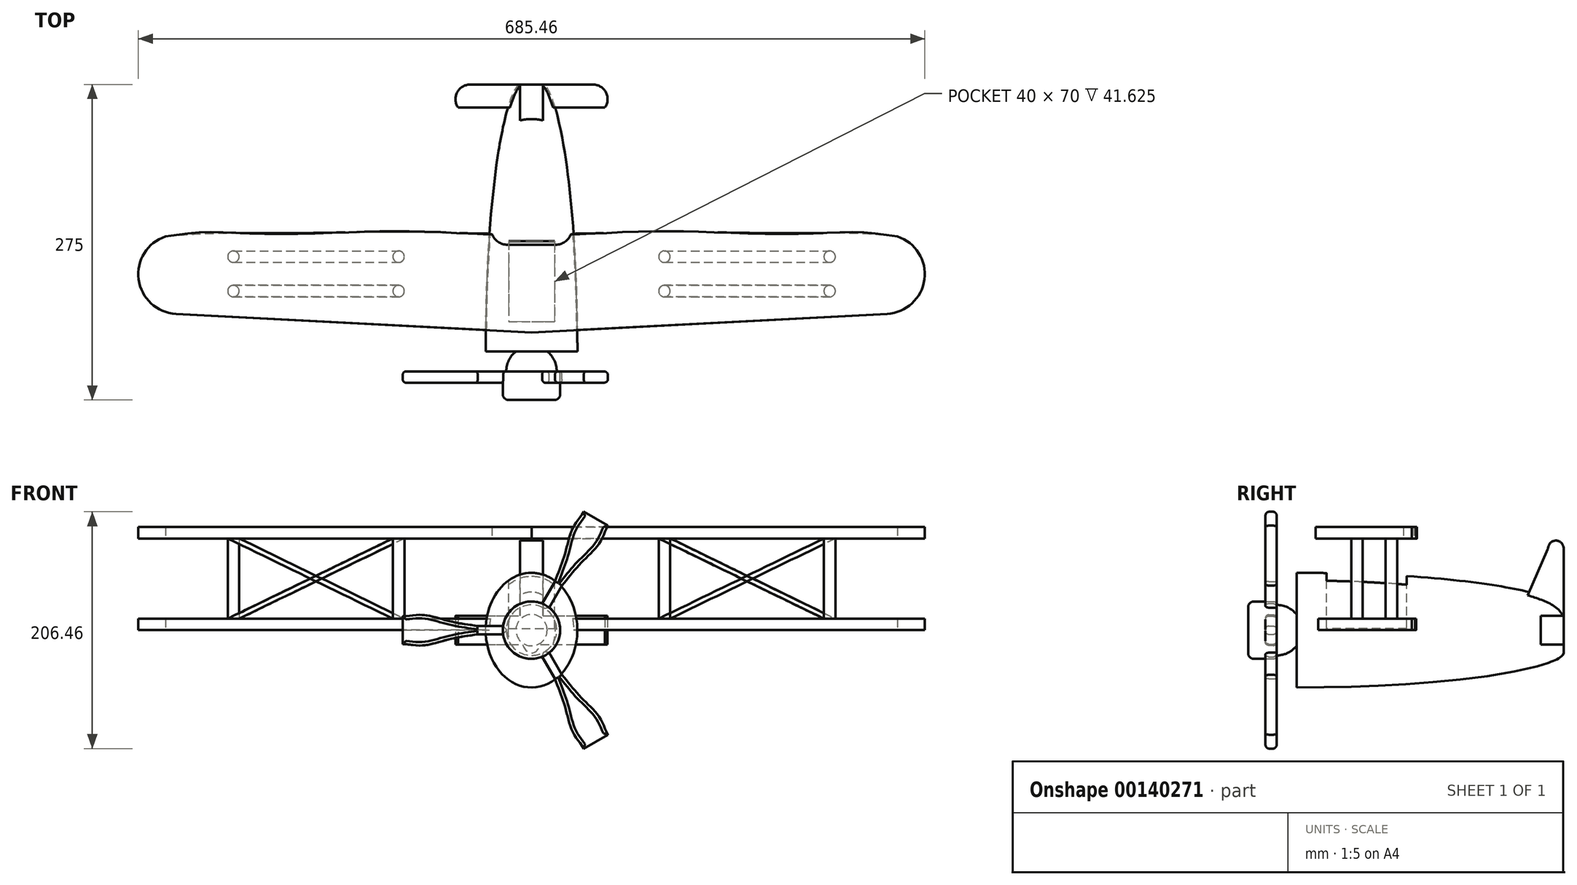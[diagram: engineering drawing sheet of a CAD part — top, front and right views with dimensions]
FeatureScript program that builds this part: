
annotation { "Feature Type Name" : "Feature", "Feature Type Description" : "" }
export const myFeature = defineFeature(function(context is Context, id is Id, definition is map)
    precondition{}
    {
        {
            var Q0;
            Q0=qCreatedBy(makeId("Front.planeOp"),FACE);
            var sketch = newSketch(context, id + "F0", { "sketchPlane" : qUnion([Q0])});
            skCircle(sketch, "E0", {"center": v(0, 0) * mm, "radius": 25 * mm});
            skSolve(sketch);
        }
        {
            var Q0;
            Q0=makeQuery(id+"F0.imprint","IMPRINT",FACE,{"disambiguationData":[TD([[makeQuery(id+"F0.imprint","IMPRINT",EDGE,{"derivedFrom":sQuery(id+"F0.wireOp",EDGE,"E0")}),1.0]])]});
            extrude(context, id + "F1", {"entities" : qUnion([Q0]), "depth" : 25 * mm});
        }
        {
            var Q0;
            Q0=makeQuery(id+"F1.opExtrude","CAP_EDGE",EDGE,{"disambiguationData":[OSD([sQuery(id+"F0.wireOp",EDGE,"E0")])],"isStart":false});
            fillet(context, id + "F2", {"entities" : qUnion([Q0]), "radius" : 5 * mm, "tangentPropagation" : true, "allowEdgeOverflow" : false});
        }
        {
            var Q0;
            Q0=qCreatedBy(makeId("Front.planeOp"),FACE);
            var sketch = newSketch(context, id + "F3", { "sketchPlane" : qUnion([Q0])});
            skArc(sketch, "E1.0", {"start": v(-24.75, 3.55) * mm, "mid": v(-25, 0) * mm, "end": v(-24.75, -3.55) * mm});
            skLineSegment(sketch, "E2", {"start": v(-124.47, 0) * mm, "end": v(45.62, 0) * mm, "construction": true});
            skLineSegment(sketch, "E3", {"start": v(-112.22, 0) * mm, "end": v(-112.22, 12.1) * mm});
            skLineSegment(sketch, "E4", {"start": v(-24.75, 3.55) * mm, "end": v(-47, 3.55) * mm});
            skFitSpline(sketch, "E5", {"points": [v(-47, 3.55) * mm, v(-69.47, 7.36) * mm, v(-95.13, 13.3) * mm, v(-112.22, 12.1) * mm], "startDerivative": vector(-60.76, 10.94) * mm, "endDerivative": vector(-54.66, -0.71) * mm});
            skLineSegment(sketch, "E6.MirrorCS", {"start": v(-112.22, 0) * mm, "end": v(-112.22, -12.1) * mm});
            skLineSegment(sketch, "E7.MirrorCS", {"start": v(-24.75, -3.55) * mm, "end": v(-47, -3.55) * mm});
            skFitSpline(sketch, "E8.MirrorCS", {"points": [v(-47, -3.55) * mm, v(-69.47, -7.36) * mm, v(-95.13, -13.3) * mm, v(-112.22, -12.1) * mm], "startDerivative": vector(-60.76, -10.94) * mm, "endDerivative": vector(-54.66, 0.71) * mm});
            skSolve(sketch);
        }
        {
            var Q0;
            Q0=makeQuery(id+"F3.imprint","IMPRINT",FACE,{"disambiguationData":[TD([[makeQuery(id+"F3.imprint","IMPRINT",EDGE,{"derivedFrom":sQuery(id+"F3.wireOp",EDGE,"E1.0")}),-1.0]])]});
            extrude(context, id + "F4", {"entities" : qUnion([Q0]), "operationType" : NewBodyOperationType.ADD, "depth" : 10 * mm});
        }
        {
            var Q0;
            Q0=makeQuery(id+"F4.opExtrude","CAP_EDGE",EDGE,{"disambiguationData":[OSD([sQuery(id+"F3.wireOp",EDGE,"E5")])],"isStart":false});
            var Q1;
            Q1=makeQuery(id+"F4.opExtrude","CAP_EDGE",EDGE,{"disambiguationData":[OSD([sQuery(id+"F3.wireOp",EDGE,"E4")])],"isStart":false});
            var Q2;
            Q2=makeQuery(id+"F4.opExtrude","CAP_EDGE",EDGE,{"disambiguationData":[OSD([sQuery(id+"F3.wireOp",EDGE,"E8.MirrorCS")])],"isStart":false});
            var Q3;
            Q3=makeQuery(id+"F4.opExtrude","CAP_EDGE",EDGE,{"disambiguationData":[OSD([sQuery(id+"F3.wireOp",EDGE,"E7.MirrorCS")])],"isStart":false});
            var Q4;
            Q4=makeQuery(id+"F4.opExtrude","CAP_EDGE",EDGE,{"disambiguationData":[OSD([sQuery(id+"F3.wireOp",EDGE,"E3"),sQuery(id+"F3.wireOp",EDGE,"E6.MirrorCS")])],"isStart":false});
            fillet(context, id + "F5", {"entities" : qUnion([Q0, Q1, Q2, Q3, Q4]), "radius" : 3 * mm, "tangentPropagation" : true, "allowEdgeOverflow" : false});
        }
        {
            var Q0;
            Q0=makeQuery(id+"F4.boolean.opBoolean","MERGE",FACE,{"derivedFrom":[makeQuery(id+"F1.opExtrude","CAP_FACE",FACE,{"disambiguationData":[OSD([sQuery(id+"F0.wireOp",EDGE,"E0")])],"isStart":true}),makeQuery(id+"F4.opExtrude","CAP_FACE",FACE,{"disambiguationData":[OSD([sQuery(id+"F3.wireOp",EDGE,"E1.0"),sQuery(id+"F3.wireOp",EDGE,"E3"),sQuery(id+"F3.wireOp",EDGE,"E4"),sQuery(id+"F3.wireOp",EDGE,"E5"),sQuery(id+"F3.wireOp",EDGE,"E6.MirrorCS"),sQuery(id+"F3.wireOp",EDGE,"E7.MirrorCS"),sQuery(id+"F3.wireOp",EDGE,"E8.MirrorCS")])],"isStart":true})]});
            fillet(context, id + "F6", {"entities" : qUnion([Q0]), "radius" : 3 * mm, "tangentPropagation" : true, "allowEdgeOverflow" : false});
        }
        {
            var Q0;
            Q0=qCreatedBy(makeId("Top.planeOp"),FACE);
            var sketch = newSketch(context, id + "F7", { "sketchPlane" : qUnion([Q0])});
            skLineSegment(sketch, "E9", {"start": v(0, -64.65) * mm, "end": v(0, 40.57) * mm});
            skSolve(sketch);
        }
        {
            var Q0;
            Q0=makeQuery(id+"F1.opExtrude","SWEPT_BODY",BODY,{"disambiguationData":[OSD([sQuery(id+"F0.wireOp",EDGE,"E0")])]});
            var Q1;
            Q1=sQuery(id+"F7.wireOp",EDGE,"E9");
            circularPattern(context, id + "F8", {"entities" : qUnion([Q0]), "axis" : qUnion([Q1]), "angle" : 360 * degree, "instanceCount" : 3, "equalSpace" : true});
        }
        {
            var Q0;
            Q0=qCreatedBy(makeId("Right.planeOp"),FACE);
            var sketch = newSketch(context, id + "F9", { "sketchPlane" : qUnion([Q0])});
            skLineSegment(sketch, "E10", {"start": v(0, 0) * mm, "end": v(17.25, 0) * mm});
            skLineSegment(sketch, "E11", {"start": v(0, -22) * mm, "end": v(0, 22) * mm, "construction": true});
            skArc(sketch, "E12", {"start": v(0, -22) * mm, "mid": v(9.58, -19.8) * mm, "end": v(17.25, -13.65) * mm});
            skLineSegment(sketch, "E13", {"start": v(17.25, 0) * mm, "end": v(17.25, -13.65) * mm});
            skLineSegment(sketch, "E14", {"start": v(0, 0) * mm, "end": v(0, -22) * mm});
            skSolve(sketch);
        }
        {
            var Q0;
            Q0=makeQuery(id+"F9.imprint","IMPRINT",FACE,{"disambiguationData":[TD([[makeQuery(id+"F9.imprint","IMPRINT",EDGE,{"derivedFrom":sQuery(id+"F9.wireOp",EDGE,"E10")}),-1.0]])]});
            var Q1;
            Q1=sQuery(id+"F9.wireOp",EDGE,"E10");
            revolve(context, id + "F10", {"operationType" : NewBodyOperationType.ADD, "entities" : qUnion([Q0]), "axis" : qUnion([Q1]), "revolveType" : RevolveType.FULL});
        }
        {
            var Q0;
            Q0=makeQuery(id+"F10.opRevolve","SWEPT_FACE",FACE,{"disambiguationData":[OSD([sQuery(id+"F9.wireOp",EDGE,"E13")])]});
            var sketch = newSketch(context, id + "F11", { "sketchPlane" : qUnion([Q0])});
            skEllipse(sketch, "E15", {"center": v(0, 0) * mm, "majorRadius": 50 * mm, "minorRadius": 40 * mm, "majorAxis": v(0, 1)});
            skSolve(sketch);
        }
        {
            var Q0;
            Q0=qCreatedBy(makeId("Front.planeOp"),FACE);
            cPlane(context, id + "F12", {"entities" : qUnion([Q0]), "cplaneType" : CPlaneType.OFFSET, "offset" : 250 * mm, "oppositeDirection" : true, "width" : 150 * mm, "height" : 150 * mm});
        }
        {
            var Q0;
            Q0=qCreatedBy(id+"F12.planeOp",FACE);
            var sketch = newSketch(context, id + "F13", { "sketchPlane" : qUnion([Q0])});
            skEllipse(sketch, "E16", {"center": v(0, 0) * mm, "majorRadius": 20 * mm, "minorRadius": 10 * mm, "majorAxis": v(0, 1)});
            skSolve(sketch);
        }
        {
            var Q1;
            Q1 = qSketchRegion(id + "F11", true);
            var Q2;
            Q2 = qSketchRegion(id + "F13", true);
            loft(context, id + "F14", {"operationType" : NewBodyOperationType.ADD, "startCondition" : LoftEndDerivativeType.NORMAL_TO_PROFILE, "startMagnitude" : 2, "endCondition" : LoftEndDerivativeType.TANGENT_TO_PROFILE, "endMagnitude" : 1, "sheetProfilesArray" : [{ "sheetProfileEntities" : qUnion([Q1]) }, { "sheetProfileEntities" : qUnion([Q2]) }]});
        }
        {
            var Q0;
            Q0=qCreatedBy(makeId("Top.planeOp"),FACE);
            var sketch = newSketch(context, id + "F15", { "sketchPlane" : qUnion([Q0])});
            skFitSpline(sketch, "E17.0", {"points": [v(-10, 250) * mm, v(-3.33, 250) * mm, v(3.33, 250) * mm, v(10, 250) * mm], "construction": true});
            skLineSegment(sketch, "E18", {"start": v(0, 273.6) * mm, "end": v(0, 147.57) * mm, "construction": true});
            skLineSegment(sketch, "E19", {"start": v(0, 250) * mm, "end": v(-53.66, 250) * mm});
            skLineSegment(sketch, "E20", {"start": v(-63.9, 229.96) * mm, "end": v(0, 229.96) * mm});
            skArc(sketch, "E21", {"start": v(-53.66, 250) * mm, "mid": v(-64.91, 243.11) * mm, "end": v(-63.9, 229.96) * mm});
            skFitSpline(sketch, "E22.MirrorCS", {"points": [v(10, 250) * mm, v(3.33, 250) * mm, v(-3.33, 250) * mm, v(-10, 250) * mm], "construction": true});
            skArc(sketch, "E23.MirrorCS", {"start": v(53.66, 250) * mm, "mid": v(64.91, 243.11) * mm, "end": v(63.9, 229.96) * mm});
            skLineSegment(sketch, "E24.MirrorCS", {"start": v(0, 250) * mm, "end": v(53.66, 250) * mm});
            skLineSegment(sketch, "E25.MirrorCS", {"start": v(63.9, 229.96) * mm, "end": v(0, 229.96) * mm});
            skSolve(sketch);
        }
        {
            var Q0;
            Q0=makeQuery(id+"F15.imprint","IMPRINT",FACE,{"disambiguationData":[TD([[makeQuery(id+"F15.imprint","IMPRINT",EDGE,{"derivedFrom":sQuery(id+"F15.wireOp",EDGE,"E19")}),1.0]])]});
            extrude(context, id + "F16", {"entities" : qUnion([Q0]), "operationType" : NewBodyOperationType.ADD, "endBound" : BoundingType.SYMMETRIC, "depth" : 25 * mm});
        }
        {
            var Q0;
            Q0=qCreatedBy(makeId("Right.planeOp"),FACE);
            var sketch = newSketch(context, id + "F17", { "sketchPlane" : qUnion([Q0])});
            skFitSpline(sketch, "E26.0", {"points": [v(250, 12.5) * mm, v(250, 15) * mm, v(250, 17.5) * mm, v(250, 20) * mm], "construction": true});
            skFitSpline(sketch, "E27.0", {"points": [v(250, -12.5) * mm, v(250, -15) * mm, v(250, -17.5) * mm, v(250, -20) * mm], "construction": true});
            skLineSegment(sketch, "E28.0", {"start": v(250, 12.5) * mm, "end": v(250, -12.5) * mm, "construction": true});
            skLineSegment(sketch, "E29", {"start": v(250, 12.5) * mm, "end": v(250, 71.39) * mm});
            skPoint(sketch, "E29.endSnap0", {"position": v(250, 0) * mm});
            skArc(sketch, "E30", {"start": v(250, 71.39) * mm, "mid": v(243.6, 78.12) * mm, "end": v(236.55, 72.06) * mm});
            skLineSegment(sketch, "E31", {"start": v(236.16, 70.57) * mm, "end": v(215.93, 23.8) * mm});
            skLineSegment(sketch, "E32", {"start": v(250, 12.5) * mm, "end": v(209.86, 12.5) * mm});
            skLineSegment(sketch, "E33", {"start": v(215.74, 23.4) * mm, "end": v(209.86, 12.5) * mm});
            skPoint(sketch, "E34.visualSharp", {"position": v(236.51, 71.39) * mm});
            skArc(sketch, "E34.filletArc", {"start": v(236.16, 70.57) * mm, "mid": v(236.41, 71.3) * mm, "end": v(236.55, 72.06) * mm});
            skPoint(sketch, "E35.visualSharp", {"position": v(215.85, 23.6) * mm});
            skArc(sketch, "E35.filletArc", {"start": v(215.74, 23.4) * mm, "mid": v(215.84, 23.6) * mm, "end": v(215.93, 23.8) * mm});
            skSolve(sketch);
        }
        {
            var Q0;
            Q0=makeQuery(id+"F17.imprint","IMPRINT",FACE,{"disambiguationData":[TD([[makeQuery(id+"F17.imprint","IMPRINT",EDGE,{"derivedFrom":sQuery(id+"F17.wireOp",EDGE,"E29")}),1.0]])]});
            extrude(context, id + "F18", {"entities" : qUnion([Q0]), "operationType" : NewBodyOperationType.ADD, "endBound" : BoundingType.SYMMETRIC, "depth" : 20 * mm});
        }
        {
            var Q0;
            Q0=qCreatedBy(makeId("Top.planeOp"),FACE);
            cPlane(context, id + "F19", {"entities" : qUnion([Q0]), "cplaneType" : CPlaneType.OFFSET, "offset" : 70 * mm, "width" : 150 * mm, "height" : 150 * mm});
        }
        {
            var Q0;
            Q0=qCreatedBy(id+"F19.planeOp",FACE);
            var sketch = newSketch(context, id + "F20", { "sketchPlane" : qUnion([Q0])});
            skLineSegment(sketch, "E36.bottom", {"start": v(-20, 113.36) * mm, "end": v(20, 113.36) * mm});
            skLineSegment(sketch, "E36.top", {"start": v(-20, 43.36) * mm, "end": v(20, 43.36) * mm});
            skLineSegment(sketch, "E36.left", {"start": v(-20, 113.36) * mm, "end": v(-20, 43.36) * mm});
            skLineSegment(sketch, "E36.right", {"start": v(20, 113.36) * mm, "end": v(20, 43.36) * mm});
            skSolve(sketch);
        }
        {
            var Q0;
            Q0=makeQuery(id+"F20.imprint","IMPRINT",FACE,{"disambiguationData":[TD([[makeQuery(id+"F20.imprint","IMPRINT",EDGE,{"derivedFrom":sQuery(id+"F20.wireOp",EDGE,"E36.bottom")}),-1.0]])]});
            extrude(context, id + "F21", {"entities" : qUnion([Q0]), "operationType" : NewBodyOperationType.REMOVE, "oppositeDirection" : true, "depth" : 68.56 * mm});
        }
        {
            var Q0;
            Q0=qCreatedBy(makeId("Top.planeOp"),FACE);
            var sketch = newSketch(context, id + "F22", { "sketchPlane" : qUnion([Q0])});
            skLineSegment(sketch, "E37", {"start": v(26.98, 35.3) * mm, "end": v(309.9, 50.13) * mm});
            skArc(sketch, "E38", {"start": v(309.9, 50.13) * mm, "mid": v(342.42, 80.12) * mm, "end": v(318.96, 117.62) * mm});
            skFitSpline(sketch, "E39", {"points": [v(318.96, 117.62) * mm, v(231.3, 120.45) * mm, v(157.79, 121.16) * mm, v(87.8, 121.16) * mm, v(26.98, 120.21) * mm], "startDerivative": vector(-387.66, 39.94) * mm, "endDerivative": vector(-140.96, 8.48) * mm});
            skLineSegment(sketch, "E40", {"start": v(26.98, 120.21) * mm, "end": v(26.98, 35.3) * mm});
            skLineSegment(sketch, "E41.MirrorCS", {"start": v(-26.98, 120.21) * mm, "end": v(-26.98, 35.3) * mm});
            skLineSegment(sketch, "E42.MirrorCS", {"start": v(-26.98, 35.3) * mm, "end": v(-309.9, 50.13) * mm});
            skFitSpline(sketch, "E43.MirrorCS", {"points": [v(-318.96, 117.62) * mm, v(-231.3, 120.45) * mm, v(-157.79, 121.16) * mm, v(-87.8, 121.16) * mm, v(-26.98, 120.21) * mm], "startDerivative": vector(387.66, 39.94) * mm, "endDerivative": vector(140.96, 8.48) * mm});
            skArc(sketch, "E44.MirrorCS", {"start": v(-309.9, 50.13) * mm, "mid": v(-342.42, 80.12) * mm, "end": v(-318.96, 117.62) * mm});
            skSolve(sketch);
        }
        {
            var Q0;
            Q0=makeQuery(id+"F22.imprint","IMPRINT",FACE,{"disambiguationData":[TD([[makeQuery(id+"F22.imprint","IMPRINT",EDGE,{"derivedFrom":sQuery(id+"F22.wireOp",EDGE,"E41.MirrorCS")}),-1.0]])]});
            var Q1;
            Q1=makeQuery(id+"F22.imprint","IMPRINT",FACE,{"disambiguationData":[TD([[makeQuery(id+"F22.imprint","IMPRINT",EDGE,{"derivedFrom":sQuery(id+"F22.wireOp",EDGE,"E37")}),1.0]])]});
            extrude(context, id + "F23", {"entities" : qUnion([Q0, Q1]), "operationType" : NewBodyOperationType.ADD, "depth" : 10 * mm});
        }
        {
            var Q0;
            Q0=makeQuery(id+"F23.opExtrude","CAP_FACE",FACE,{"disambiguationData":[OSD([sQuery(id+"F22.wireOp",EDGE,"E37"),sQuery(id+"F22.wireOp",EDGE,"E38"),sQuery(id+"F22.wireOp",EDGE,"E39"),sQuery(id+"F22.wireOp",EDGE,"E40")])],"isStart":false});
            cPlane(context, id + "F24", {"entities" : qUnion([Q0]), "cplaneType" : CPlaneType.OFFSET, "offset" : 70 * mm, "width" : 150 * mm, "height" : 150 * mm});
        }
        {
            var Q0;
            Q0=qCreatedBy(id+"F24.planeOp",FACE);
            var sketch = newSketch(context, id + "F25", { "sketchPlane" : qUnion([Q0])});
            skLineSegment(sketch, "E45.0", {"start": v(0, 33.9) * mm, "end": v(309.9, 50.13) * mm});
            skLineSegment(sketch, "E46.0", {"start": v(0, 33.9) * mm, "end": v(-309.9, 50.13) * mm});
            skArc(sketch, "E47.0", {"start": v(-309.9, 50.13) * mm, "mid": v(-342.42, 80.12) * mm, "end": v(-318.96, 117.62) * mm});
            skFitSpline(sketch, "E48.0", {"points": [v(-318.96, 117.62) * mm, v(-283.48, 121.28) * mm, v(-234.6, 119.86) * mm, v(-156.78, 121.28) * mm, v(-92.83, 121.86) * mm, v(-37.72, 119.57) * mm, v(-26.98, 120.21) * mm]});
            skFitSpline(sketch, "E49.0", {"points": [v(318.96, 117.62) * mm, v(283.48, 121.28) * mm, v(234.6, 119.86) * mm, v(156.78, 121.28) * mm, v(92.83, 121.86) * mm, v(37.72, 119.57) * mm, v(26.98, 120.21) * mm]});
            skArc(sketch, "E50.0", {"start": v(309.9, 50.13) * mm, "mid": v(342.42, 80.12) * mm, "end": v(318.96, 117.62) * mm});
            skPoint(sketch, "E51.orphan", {"position": v(39.05, 35.94) * mm});
            skPoint(sketch, "E52.orphan", {"position": v(-39.05, 35.94) * mm});
            skLineSegment(sketch, "E53", {"start": v(-21, 110.42) * mm, "end": v(21, 110.42) * mm});
            skArc(sketch, "E54", {"start": v(-34.5, 120.02) * mm, "mid": v(-29.28, 113.06) * mm, "end": v(-21, 110.42) * mm});
            skArc(sketch, "E55.MirrorCS", {"start": v(34.5, 120.02) * mm, "mid": v(29.28, 113.06) * mm, "end": v(21, 110.42) * mm});
            skSolve(sketch);
        }
        {
            var Q0;
            Q0=makeQuery(id+"F25.imprint","IMPRINT",FACE,{"disambiguationData":[TD([[makeQuery(id+"F25.imprint","IMPRINT",EDGE,{"derivedFrom":sQuery(id+"F25.wireOp",EDGE,"E45.0")}),1.0]])]});
            extrude(context, id + "F26", {"entities" : qUnion([Q0]), "depth" : 10 * mm});
        }
        {
            var Q0;
            Q0=makeQuery(id+"F23.opExtrude","CAP_FACE",FACE,{"disambiguationData":[OSD([sQuery(id+"F22.wireOp",EDGE,"E37"),sQuery(id+"F22.wireOp",EDGE,"E38"),sQuery(id+"F22.wireOp",EDGE,"E39"),sQuery(id+"F22.wireOp",EDGE,"E40")])],"isStart":false});
            var sketch = newSketch(context, id + "F27", { "sketchPlane" : qUnion([Q0])});
            skCircle(sketch, "E56", {"center": v(259.83, 99.96) * mm, "radius": 5 * mm});
            skCircle(sketch, "E57", {"center": v(115.84, 99.96) * mm, "radius": 5 * mm});
            skSolve(sketch);
        }
        {
            var Q0;
            Q0 = qSketchRegion(id + "F27", true);
            extrude(context, id + "F28", {"entities" : qUnion([Q0]), "endBound" : BoundingType.UP_TO_NEXT, "depth" : 25 * mm});
        }
        {
            var Q0;
            Q0=makeQuery(id+"F23.opExtrude","CAP_FACE",FACE,{"disambiguationData":[OSD([sQuery(id+"F22.wireOp",EDGE,"E37"),sQuery(id+"F22.wireOp",EDGE,"E38"),sQuery(id+"F22.wireOp",EDGE,"E39"),sQuery(id+"F22.wireOp",EDGE,"E40")])],"isStart":false});
            var sketch = newSketch(context, id + "F29", { "sketchPlane" : qUnion([Q0])});
            skCircle(sketch, "E58.0", {"center": v(115.84, 99.96) * mm, "radius": 5 * mm});
            skSolve(sketch);
        }
        {
            var Q0;
            Q0=qCreatedBy(makeId("Front.planeOp"),FACE);
            var sketch = newSketch(context, id + "F30", { "sketchPlane" : qUnion([Q0])});
            skPoint(sketch, "E59.0", {"position": v(115.84, 10) * mm});
            skLineSegment(sketch, "E60.0", {"start": v(254.83, 80) * mm, "end": v(264.83, 80) * mm, "construction": true});
            skLineSegment(sketch, "E61", {"start": v(115.84, 10) * mm, "end": v(259.83, 80) * mm});
            skSolve(sketch);
        }
        {
            var Q0;
            Q0 = qSketchRegion(id + "F29", true);
            var Q1;
            Q1 = qConstructionFilter(qBodyType(qCreatedBy(id + "F30" ,EDGE), BodyType.WIRE), ConstructionObject.NO);
            sweep(context, id + "F31", {"profiles" : qUnion([Q0]), "path" : qUnion([Q1])});
        }
        {
            var Q0;
            Q0=makeQuery(id+"F23.opExtrude","CAP_FACE",FACE,{"disambiguationData":[OSD([sQuery(id+"F22.wireOp",EDGE,"E37"),sQuery(id+"F22.wireOp",EDGE,"E38"),sQuery(id+"F22.wireOp",EDGE,"E39"),sQuery(id+"F22.wireOp",EDGE,"E40")])],"isStart":false});
            var sketch = newSketch(context, id + "F32", { "sketchPlane" : qUnion([Q0])});
            skCircle(sketch, "E62.0", {"center": v(259.83, 99.96) * mm, "radius": 5 * mm});
            skSolve(sketch);
        }
        {
            var Q0;
            Q0=qCreatedBy(makeId("Front.planeOp"),FACE);
            var sketch = newSketch(context, id + "F33", { "sketchPlane" : qUnion([Q0])});
            skLineSegment(sketch, "E63.0", {"start": v(110.84, 80) * mm, "end": v(120.84, 80) * mm, "construction": true});
            skLineSegment(sketch, "E64.0", {"start": v(254.83, 10) * mm, "end": v(264.83, 10) * mm, "construction": true});
            skLineSegment(sketch, "E65", {"start": v(115.84, 80) * mm, "end": v(259.83, 10) * mm});
            skSolve(sketch);
        }
        {
            var Q0;
            Q0 = qSketchRegion(id + "F32", true);
            var Q1;
            Q1 = qConstructionFilter(qBodyType(qCreatedBy(id + "F33" ,EDGE), BodyType.WIRE), ConstructionObject.NO);
            sweep(context, id + "F34", {"profiles" : qUnion([Q0]), "path" : qUnion([Q1])});
        }
        {
            var Q0;
            {var subQ0=sQuery(id+"F15.wireOp",EDGE,"E25.MirrorCS");var subQ2=sQuery(id+"F15.wireOp",EDGE,"E23.MirrorCS");var subQ4=sQuery(id+"F15.wireOp",EDGE,"E20");Q0=makeQuery(id+"F16.boolean.opBoolean","SPLIT",FACE,{"disambiguationData":[TD([makeQuery(id+"F16.opExtrude","SWEPT_FACE",FACE,{"disambiguationData":[OSD([subQ2])]})])],"derivedFrom":makeQuery(id+"F16.opExtrude","SWEPT_FACE",FACE,{"disambiguationData":[OSD([subQ4,subQ0])]})});}
            cPlane(context, id + "F35", {"entities" : qUnion([Q0]), "cplaneType" : CPlaneType.OFFSET, "offset" : 145 * mm, "width" : 150 * mm, "height" : 150 * mm});
        }
        {
            var Q0;
            Q0=makeQuery(id+"F28.opExtrude","SWEPT_BODY",BODY,{"disambiguationData":[OSD([sQuery(id+"F27.wireOp",EDGE,"E56")])]});
            var Q1;
            Q1=makeQuery(id+"F34.opSweep","SWEPT_BODY",BODY,{"disambiguationData":[OSD([sQuery(id+"F32.wireOp",EDGE,"E62.0"),sQuery(id+"F33.wireOp",EDGE,"E65")])]});
            var Q2;
            Q2=makeQuery(id+"F31.opSweep","SWEPT_BODY",BODY,{"disambiguationData":[OSD([sQuery(id+"F29.wireOp",EDGE,"E58.0"),sQuery(id+"F30.wireOp",EDGE,"E61")])]});
            var Q3;
            Q3=makeQuery(id+"F28.opExtrude","SWEPT_BODY",BODY,{"disambiguationData":[OSD([sQuery(id+"F27.wireOp",EDGE,"E57")])]});
            var Q4;
            Q4=qCreatedBy(id+"F35.planeOp",FACE);
            mirror(context, id + "F36", {"entities" : qUnion([Q0, Q1, Q2, Q3]), "mirrorPlane" : qUnion([Q4])});
        }
        {
            var Q0;
            Q0=makeQuery(id+"F28.opExtrude","SWEPT_BODY",BODY,{"disambiguationData":[OSD([sQuery(id+"F27.wireOp",EDGE,"E56")])]});
            var Q1;
            Q1=makeQuery(id+"F36.opPattern","COPY",BODY,{"derivedFrom":makeQuery(id+"F28.opExtrude","SWEPT_BODY",BODY,{"disambiguationData":[OSD([sQuery(id+"F27.wireOp",EDGE,"E56")])]}),"instanceName":"1"});
            var Q2;
            Q2=makeQuery(id+"F36.opPattern","COPY",BODY,{"derivedFrom":makeQuery(id+"F31.opSweep","SWEPT_BODY",BODY,{"disambiguationData":[OSD([sQuery(id+"F29.wireOp",EDGE,"E58.0"),sQuery(id+"F30.wireOp",EDGE,"E61")])]}),"instanceName":"1"});
            var Q3;
            Q3=makeQuery(id+"F31.opSweep","SWEPT_BODY",BODY,{"disambiguationData":[OSD([sQuery(id+"F29.wireOp",EDGE,"E58.0"),sQuery(id+"F30.wireOp",EDGE,"E61")])]});
            var Q4;
            Q4=makeQuery(id+"F34.opSweep","SWEPT_BODY",BODY,{"disambiguationData":[OSD([sQuery(id+"F32.wireOp",EDGE,"E62.0"),sQuery(id+"F33.wireOp",EDGE,"E65")])]});
            var Q5;
            Q5=makeQuery(id+"F36.opPattern","COPY",BODY,{"derivedFrom":makeQuery(id+"F34.opSweep","SWEPT_BODY",BODY,{"disambiguationData":[OSD([sQuery(id+"F32.wireOp",EDGE,"E62.0"),sQuery(id+"F33.wireOp",EDGE,"E65")])]}),"instanceName":"1"});
            var Q6;
            Q6=makeQuery(id+"F28.opExtrude","SWEPT_BODY",BODY,{"disambiguationData":[OSD([sQuery(id+"F27.wireOp",EDGE,"E57")])]});
            var Q7;
            Q7=makeQuery(id+"F36.opPattern","COPY",BODY,{"derivedFrom":makeQuery(id+"F28.opExtrude","SWEPT_BODY",BODY,{"disambiguationData":[OSD([sQuery(id+"F27.wireOp",EDGE,"E57")])]}),"instanceName":"1"});
            var Q8;
            Q8=qCreatedBy(makeId("Right.planeOp"),FACE);
            mirror(context, id + "F37", {"entities" : qUnion([Q0, Q1, Q2, Q3, Q4, Q5, Q6, Q7]), "mirrorPlane" : qUnion([Q8])});
        }
    });
